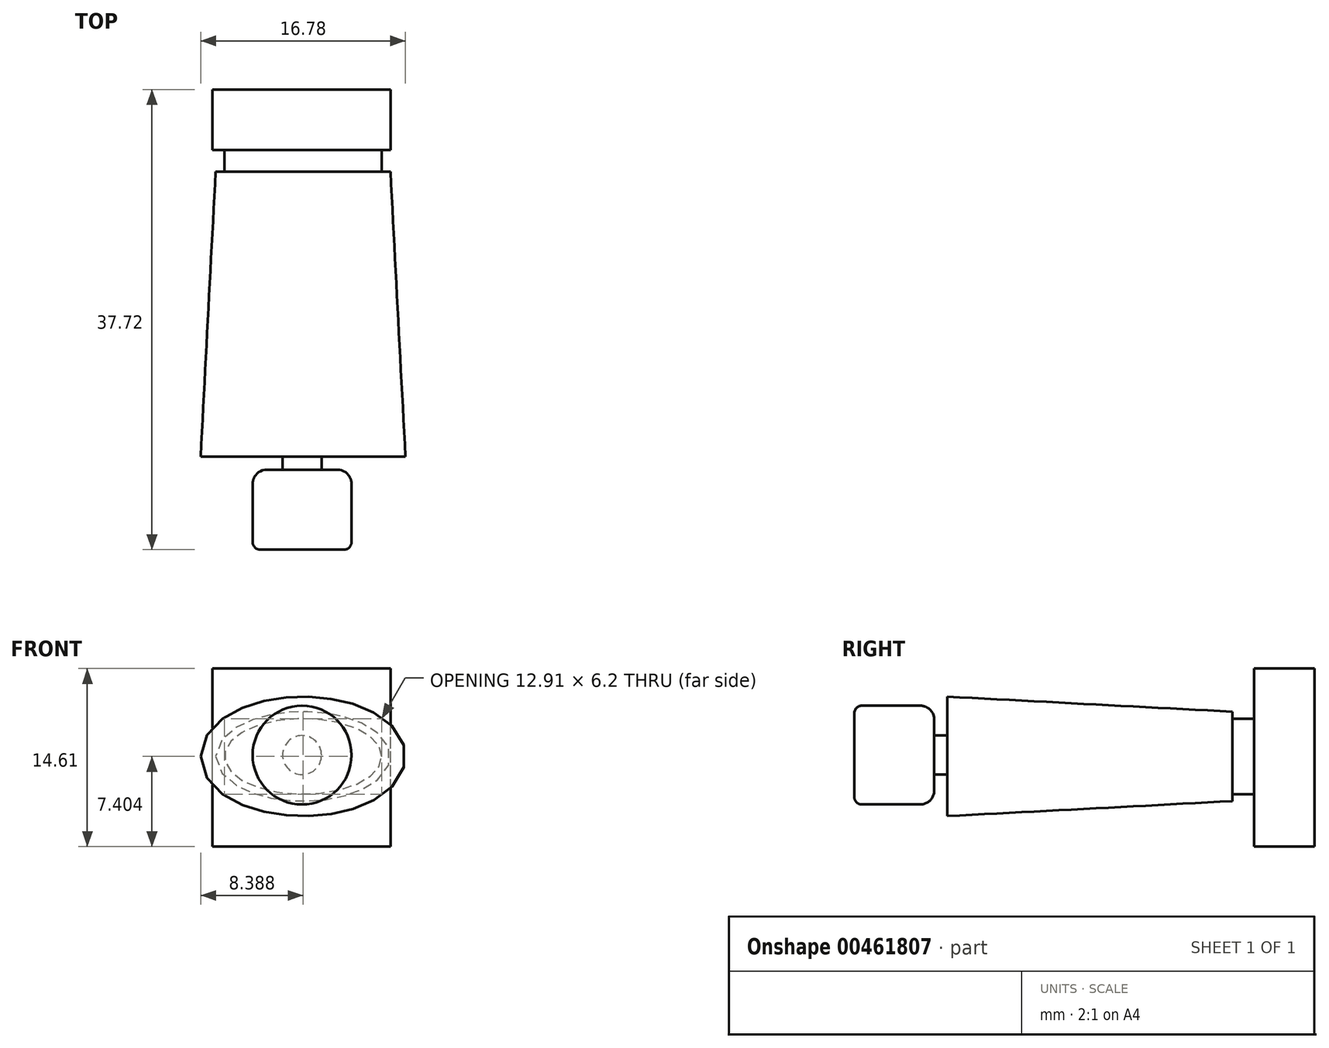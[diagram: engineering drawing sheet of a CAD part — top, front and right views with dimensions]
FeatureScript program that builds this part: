
annotation { "Feature Type Name" : "Feature", "Feature Type Description" : "" }
export const myFeature = defineFeature(function(context is Context, id is Id, definition is map)
    precondition{}
    {
        {
            var Q0;
            Q0=qCreatedBy(makeId("Front.planeOp"),FACE);
            var sketch = newSketch(context, id + "F0", { "sketchPlane" : qUnion([Q0])});
            skLineSegment(sketch, "E0.bottom", {"start": v(0, 0) * mm, "end": v(-14.6, 0) * mm});
            skLineSegment(sketch, "E0.top", {"start": v(0, 14.6) * mm, "end": v(-14.6, 14.6) * mm});
            skLineSegment(sketch, "E0.left", {"start": v(0, 0) * mm, "end": v(0, 14.6) * mm});
            skLineSegment(sketch, "E0.right", {"start": v(-14.6, 0) * mm, "end": v(-14.6, 14.6) * mm});
            skEllipse(sketch, "E1", {"center": v(-7.2, 7.54) * mm, "majorRadius": 6.36 * mm, "minorRadius": 3.94 * mm, "majorAxis": v(1, 0)});
            skSolve(sketch);
        }
        {
            var Q0;
            Q0=makeQuery(id+"F0.imprint","IMPRINT",FACE,{"disambiguationData":[TD([[makeQuery(id+"F0.imprint","IMPRINT",EDGE,{"derivedFrom":sQuery(id+"F0.wireOp",EDGE,"E0.bottom")}),-1.0]])]});
            var Q1;
            Q1=makeQuery(id+"F0.imprint","IMPRINT",FACE,{"disambiguationData":[TD([[makeQuery(id+"F0.imprint","IMPRINT",EDGE,{"derivedFrom":sQuery(id+"F0.wireOp",EDGE,"E1")}),1.0]])]});
            extrude(context, id + "F1", {"entities" : qUnion([Q0, Q1]), "depth" : 4.95 * mm});
        }
        {
            var Q0;
            Q0=makeQuery(id+"F1.opExtrude","CAP_FACE",FACE,{"disambiguationData":[OSD([sQuery(id+"F0.wireOp",EDGE,"E0.bottom"),sQuery(id+"F0.wireOp",EDGE,"E0.top"),sQuery(id+"F0.wireOp",EDGE,"E0.left"),sQuery(id+"F0.wireOp",EDGE,"E0.right")])],"isStart":false});
            var sketch = newSketch(context, id + "F2", { "sketchPlane" : qUnion([Q0])});
            skEllipse(sketch, "E2", {"center": v(-7.16, 7.4) * mm, "majorRadius": 6.45 * mm, "minorRadius": 3.1 * mm, "majorAxis": v(1, 0)});
            skSolve(sketch);
        }
        {
            var Q0;
            Q0=makeQuery(id+"F2.imprint","IMPRINT",FACE,{"disambiguationData":[TD([[makeQuery(id+"F2.imprint","IMPRINT",EDGE,{"derivedFrom":sQuery(id+"F2.wireOp",EDGE,"E2")}),1.0]])]});
            extrude(context, id + "F3", {"entities" : qUnion([Q0]), "operationType" : NewBodyOperationType.ADD, "depth" : 1.78 * mm});
        }
        {
            var Q0;
            Q0=makeQuery(id+"F3.opExtrude","CAP_FACE",FACE,{"disambiguationData":[OSD([sQuery(id+"F2.wireOp",EDGE,"E2")])],"isStart":false});
            var sketch = newSketch(context, id + "F4", { "sketchPlane" : qUnion([Q0])});
            skEllipse(sketch, "E3", {"center": v(-7.16, 7.4) * mm, "majorRadius": 7.17 * mm, "minorRadius": 3.67 * mm, "majorAxis": v(1, 0)});
            skSolve(sketch);
        }
        {
            var Q0;
            Q0=makeQuery(id+"F4.imprint","IMPRINT",FACE,{"disambiguationData":[TD([[makeQuery(id+"F4.imprint","IMPRINT",EDGE,{"derivedFrom":makeQuery(id+"F3.opExtrude","CAP_EDGE",EDGE,{"disambiguationData":[OSD([sQuery(id+"F2.wireOp",EDGE,"E2")])],"isStart":false})}),1.0]])]});
            var Q1;
            Q1=makeQuery(id+"F4.imprint","IMPRINT",FACE,{"disambiguationData":[TD([[makeQuery(id+"F4.imprint","IMPRINT",EDGE,{"derivedFrom":sQuery(id+"F4.wireOp",EDGE,"E3")}),1.0]])]});
            extrude(context, id + "F5", {"entities" : qUnion([Q0, Q1]), "operationType" : NewBodyOperationType.ADD, "depth" : 23.37 * mm, "hasDraft" : true, "draftAngle" : 3 * degree});
        }
        {
            var Q0;
            Q0=makeQuery(id+"F5.opExtrude","CAP_FACE",FACE,{"disambiguationData":[OSD([sQuery(id+"F4.wireOp",EDGE,"E3")])],"isStart":false});
            var sketch = newSketch(context, id + "F6", { "sketchPlane" : qUnion([Q0])});
            skCircle(sketch, "E4", {"center": v(-7.24, 7.51) * mm, "radius": 1.6 * mm});
            skSolve(sketch);
        }
        {
            var Q0;
            Q0 = qSketchRegion(id + "F6", true);
            extrude(context, id + "F7", {"entities" : qUnion([Q0]), "operationType" : NewBodyOperationType.ADD, "depth" : 1.07 * mm});
        }
        {
            var Q0;
            Q0=makeQuery(id+"F7.opExtrude","CAP_FACE",FACE,{"disambiguationData":[OSD([sQuery(id+"F6.wireOp",EDGE,"E4")])],"isStart":false});
            var sketch = newSketch(context, id + "F8", { "sketchPlane" : qUnion([Q0])});
            skCircle(sketch, "E5", {"center": v(-7.24, 7.51) * mm, "radius": 4.05 * mm});
            skSolve(sketch);
        }
        {
            var Q0;
            Q0 = qSketchRegion(id + "F8", true);
            extrude(context, id + "F9", {"entities" : qUnion([Q0]), "operationType" : NewBodyOperationType.ADD, "depth" : 6.55 * mm});
        }
        {
            var Q0;
            Q0=makeQuery(id+"F9.opExtrude","CAP_EDGE",EDGE,{"disambiguationData":[OSD([sQuery(id+"F8.wireOp",EDGE,"E5")])],"isStart":true});
            fillet(context, id + "F10", {"entities" : qUnion([Q0]), "radius" : 1.17 * mm, "tangentPropagation" : true, "allowEdgeOverflow" : false});
        }
        {
            var Q0;
            Q0=makeQuery(id+"F9.opExtrude","CAP_EDGE",EDGE,{"disambiguationData":[OSD([sQuery(id+"F8.wireOp",EDGE,"E5")])],"isStart":false});
            fillet(context, id + "F11", {"entities" : qUnion([Q0]), "radius" : 0.61 * mm, "tangentPropagation" : true, "allowEdgeOverflow" : false});
        }
    });
